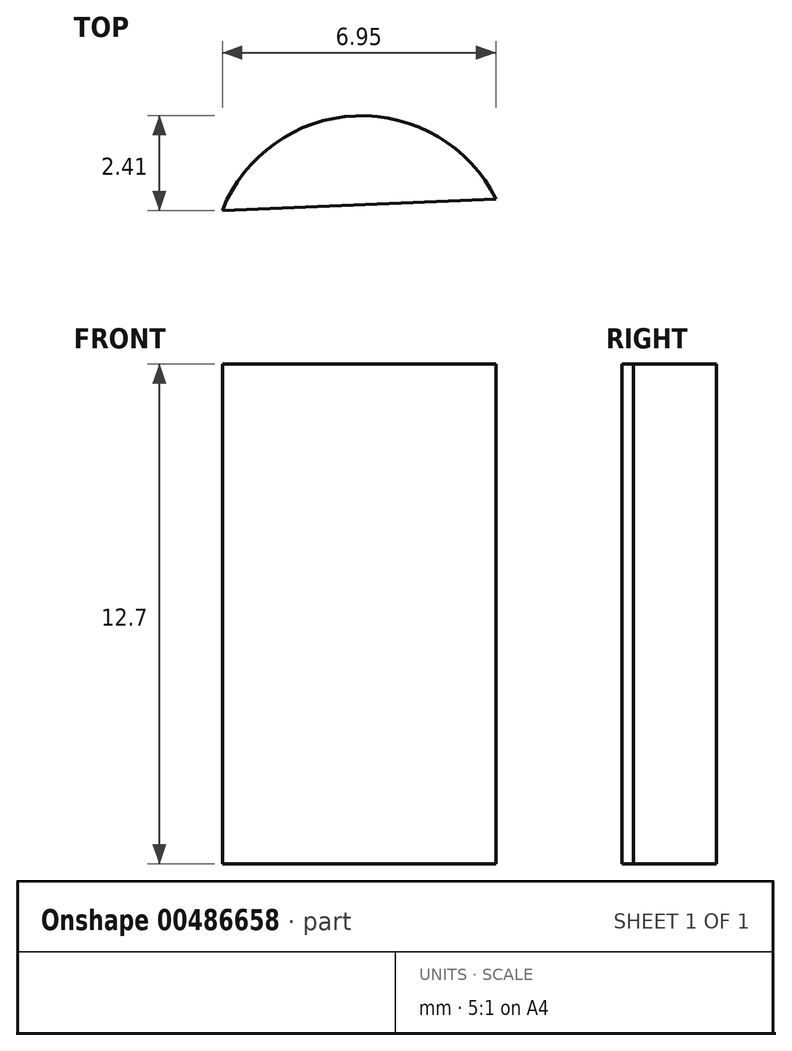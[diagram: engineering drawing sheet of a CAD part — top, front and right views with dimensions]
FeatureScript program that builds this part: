
annotation { "Feature Type Name" : "Feature", "Feature Type Description" : "" }
export const myFeature = defineFeature(function(context is Context, id is Id, definition is map)
    precondition{}
    {
        {
            var Q0;
            Q0=qCreatedBy(makeId("Top.planeOp"),FACE);
            var sketch = newSketch(context, id + "F0", { "sketchPlane" : qUnion([Q0])});
            skLineSegment(sketch, "E0", {"start": v(-83.1, 28.17) * mm, "end": v(-83.1, -9.93) * mm});
            skLineSegment(sketch, "E1", {"start": v(221.44, 15.47) * mm, "end": v(221.44, 2.77) * mm});
            skLineSegment(sketch, "E2", {"start": v(-83.1, 28.17) * mm, "end": v(221.44, 15.47) * mm});
            skLineSegment(sketch, "E3", {"start": v(-83.1, -9.93) * mm, "end": v(221.44, 2.77) * mm});
            skSolve(sketch);
        }
        {
            var Q0;
            Q0 = qSketchRegion(id + "F0", true);
            extrude(context, id + "F1", {"entities" : qUnion([Q0]), "depth" : 12.7 * mm});
        }
        {
            var Q0;
            Q0=makeQuery(id+"F1.opExtrude","CAP_FACE",FACE,{"disambiguationData":[OSD([sQuery(id+"F0.wireOp",EDGE,"E0"),sQuery(id+"F0.wireOp",EDGE,"E1"),sQuery(id+"F0.wireOp",EDGE,"E2"),sQuery(id+"F0.wireOp",EDGE,"E3")])],"isStart":false});
            var sketch = newSketch(context, id + "F2", { "sketchPlane" : qUnion([Q0])});
            skArc(sketch, "E4", {"start": v(193.14, 16.65) * mm, "mid": v(196.52, 14.25) * mm, "end": v(200.1, 16.36) * mm});
            skLineSegment(sketch, "E5", {"start": v(221.44, 9.12) * mm, "end": v(213.35, 9.12) * mm});
            skArc(sketch, "E6.MirrorCS", {"start": v(193.14, 1.6) * mm, "mid": v(196.52, 4) * mm, "end": v(200.1, 1.88) * mm});
            skSolve(sketch);
        }
        {
            var Q0;
            Q0 = qSketchRegion(id + "F2", true);
            var Q1;
            {var subQ0=sQuery(id+"F2.wireOp",EDGE,"E4");Q1=makeQuery(id+"F2.imprint","IMPRINT",FACE,{"disambiguationData":[TD([[makeQuery(id+"F2.imprint","IMPRINT",EDGE,{"derivedFrom":subQ0}),1.0]])]});}
            var Q2;
            {var subQ0=sQuery(id+"F2.wireOp",EDGE,"E6.MirrorCS");Q2=makeQuery(id+"F2.imprint","IMPRINT",FACE,{"disambiguationData":[TD([[makeQuery(id+"F2.imprint","IMPRINT",EDGE,{"derivedFrom":subQ0}),-1.0]])]});}
            extrude(context, id + "F3", {"entities" : qUnion([Q0, Q1, Q2]), "operationType" : NewBodyOperationType.REMOVE, "oppositeDirection" : true, "depth" : 25.4 * mm});
        }
        {
            var Q0;
            {var subQ0=sQuery(id+"F0.wireOp",EDGE,"E0");var subQ1=sQuery(id+"F0.wireOp",EDGE,"E3");Q0=makeQuery(id+"F3.boolean.opBoolean","SPLIT",FACE,{"disambiguationData":[TD([makeQuery(id+"F1.opExtrude","SWEPT_FACE",FACE,{"disambiguationData":[OSD([subQ0])]})])],"derivedFrom":makeQuery(id+"F1.opExtrude","SWEPT_FACE",FACE,{"disambiguationData":[OSD([subQ1])]})});}
            var sketch = newSketch(context, id + "F4", { "sketchPlane" : qUnion([Q0])});
            skLineSegment(sketch, "E7", {"start": v(-83.44, 6.35) * mm, "end": v(-7.24, 6.35) * mm});
            skCircle(sketch, "E8", {"center": v(-7.24, 6.35) * mm, "radius": 3.18 * mm});
            skSolve(sketch);
        }
        {
            var Q0;
            Q0=makeQuery(id+"F4.imprint","IMPRINT",FACE,{"disambiguationData":[TD([[makeQuery(id+"F4.imprint","IMPRINT",EDGE,{"derivedFrom":sQuery(id+"F4.wireOp",EDGE,"E8")}),1.0]])]});
            extrude(context, id + "F5", {"entities" : qUnion([Q0]), "operationType" : NewBodyOperationType.REMOVE, "oppositeDirection" : true, "depth" : 50.8 * mm});
        }
    });
